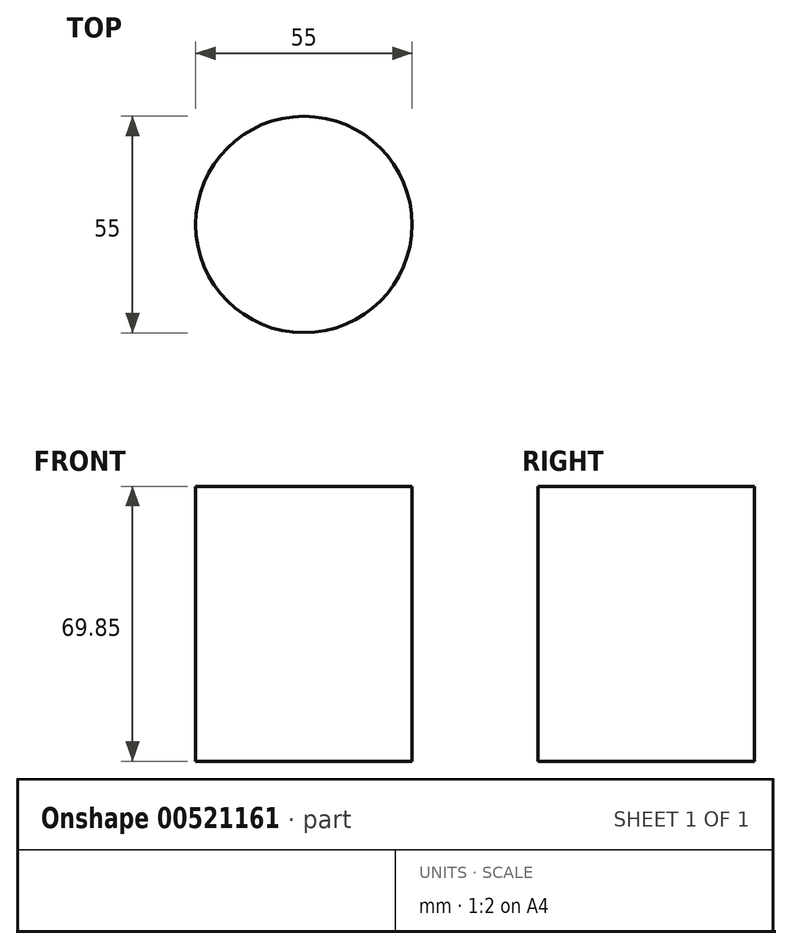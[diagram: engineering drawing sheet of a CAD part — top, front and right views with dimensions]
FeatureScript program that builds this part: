
annotation { "Feature Type Name" : "Feature", "Feature Type Description" : "" }
export const myFeature = defineFeature(function(context is Context, id is Id, definition is map)
    precondition{}
    {
        {
            var Q0;
            Q0=qCreatedBy(makeId("Top.planeOp"),FACE);
            var sketch = newSketch(context, id + "F0", { "sketchPlane" : qUnion([Q0])});
            skCircle(sketch, "E0", {"center": v(0, 0) * mm, "radius": 27.5 * mm});
            skSolve(sketch);
        }
        {
            var Q0;
            Q0=makeQuery(id+"F0.imprint","IMPRINT",FACE,{"disambiguationData":[TD([[makeQuery(id+"F0.imprint","IMPRINT",EDGE,{"derivedFrom":sQuery(id+"F0.wireOp",EDGE,"E0")}),1.0]])]});
            extrude(context, id + "F1", {"entities" : qUnion([Q0]), "depth" : 69.85 * mm, "offsetDistance" : 25.4 * mm});
        }
    });
